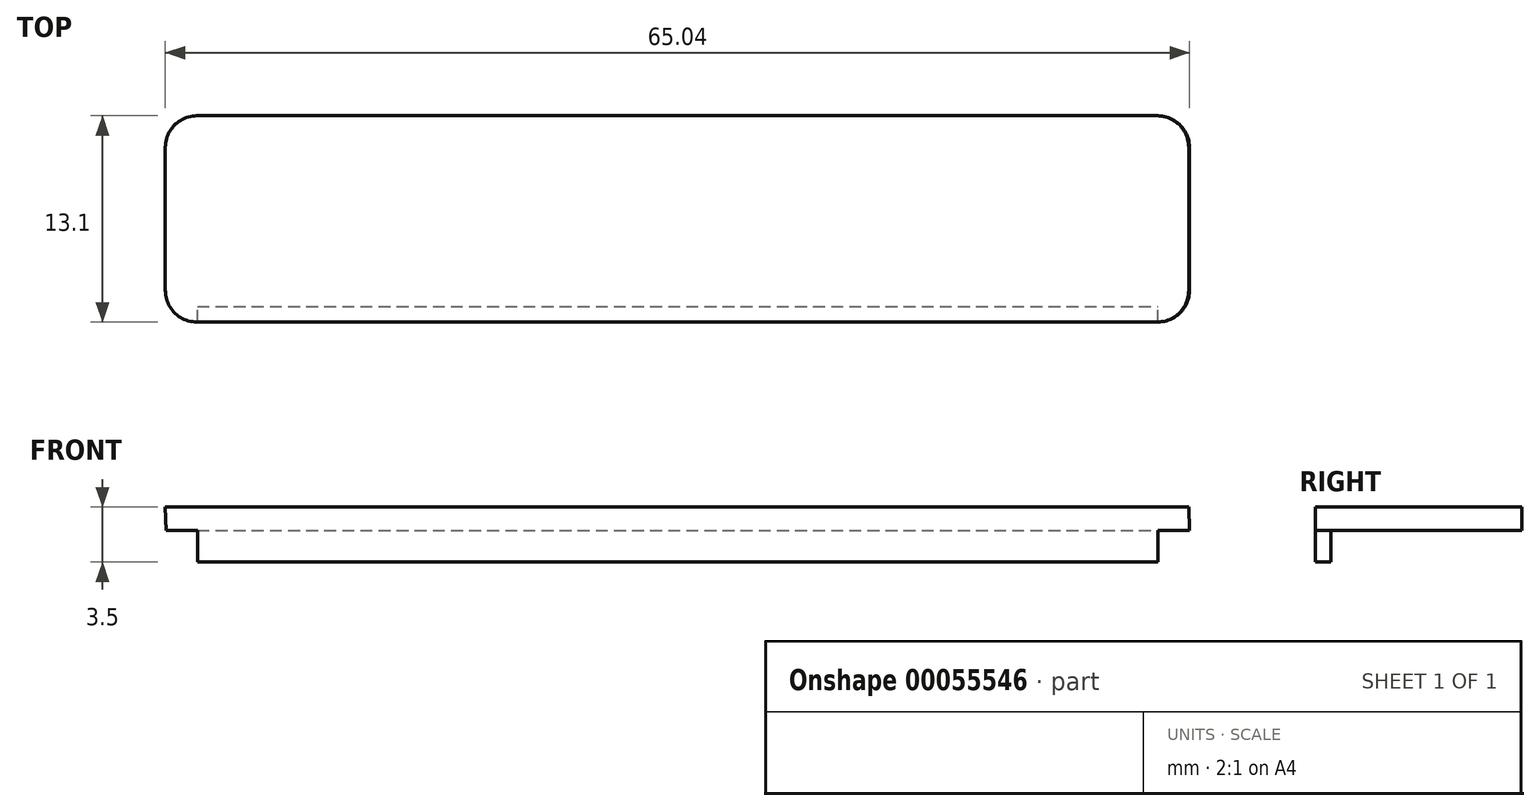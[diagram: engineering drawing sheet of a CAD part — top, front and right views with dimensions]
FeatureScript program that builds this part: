
annotation { "Feature Type Name" : "Feature", "Feature Type Description" : "" }
export const myFeature = defineFeature(function(context is Context, id is Id, definition is map)
    precondition{}
    {
        {
            var Q0;
            Q0=qCreatedBy(makeId("Front.planeOp"),FACE);
            var sketch = newSketch(context, id + "F0", { "sketchPlane" : qUnion([Q0])});
            skLineSegment(sketch, "E0", {"start": v(-42.25, 39.93) * mm, "end": v(22.75, 39.93) * mm});
            skLineSegment(sketch, "E1", {"start": v(-42.2, 38.43) * mm, "end": v(22.8, 38.43) * mm});
            skLineSegment(sketch, "E2", {"start": v(22.75, 39.93) * mm, "end": v(22.8, 38.43) * mm});
            skLineSegment(sketch, "E3", {"start": v(-42.25, 39.93) * mm, "end": v(-42.2, 38.43) * mm});
            skSolve(sketch);
        }
        {
            var Q0;
            {var subQ0=sQuery(id+"F0.wireOp",EDGE,"JaEvdv6h-OzHi-lbwa-UNxS-Qd7MtqvRkv5U");Q0=makeQuery(id+"F0.imprint","IMPRINT",FACE,{"disambiguationData":[TD([[makeQuery(id+"F0.imprint","IMPRINT",EDGE,{"derivedFrom":subQ0}),-1.0]])]});}
            var Q1;
            Q1=makeQuery(id+"F0.imprint","IMPRINT",FACE,{"disambiguationData":[TD([[makeQuery(id+"F0.imprint","IMPRINT",EDGE,{"derivedFrom":sQuery(id+"F0.wireOp",EDGE,"E1")}),1.0]])]});
            var Q2;
            {var subQ0=sQuery(id+"F0.wireOp",EDGE,"vx9o1PK7-6SiN-EeFp-MCv7-DjHtIqDTatKx");Q2=makeQuery(id+"F0.imprint","IMPRINT",FACE,{"disambiguationData":[TD([[makeQuery(id+"F0.imprint","IMPRINT",EDGE,{"derivedFrom":subQ0}),1.0]])]});}
            extrude(context, id + "F1", {"entities" : qUnion([Q0, Q1, Q2]), "depth" : 13.1 * mm});
        }
        {
            var Q0;
            Q0=makeQuery(id+"F1.opExtrude","SWEPT_FACE",FACE,{"disambiguationData":[OSD([sQuery(id+"F0.wireOp",EDGE,"E1")])]});
            var sketch = newSketch(context, id + "F2", { "sketchPlane" : qUnion([Q0])});
            skLineSegment(sketch, "E4.bottom", {"start": v(-40.2, 13.1) * mm, "end": v(20.8, 13.1) * mm});
            skLineSegment(sketch, "E4.top", {"start": v(-40.2, 12.1) * mm, "end": v(20.8, 12.1) * mm});
            skLineSegment(sketch, "E5", {"start": v(-40.2, 13.1) * mm, "end": v(-40.2, 12.1) * mm});
            skLineSegment(sketch, "E6", {"start": v(20.8, 13.1) * mm, "end": v(20.8, 12.1) * mm});
            skSolve(sketch);
        }
        {
            var Q0;
            Q0=makeQuery(id+"F1.opExtrude","CAP_EDGE",EDGE,{"disambiguationData":[OSD([sQuery(id+"F0.wireOp",EDGE,"E3")])],"isStart":false});
            var Q1;
            Q1=makeQuery(id+"F1.opExtrude","CAP_EDGE",EDGE,{"disambiguationData":[OSD([sQuery(id+"F0.wireOp",EDGE,"E2")])],"isStart":false});
            var Q2;
            Q2=makeQuery(id+"F1.opExtrude","CAP_EDGE",EDGE,{"disambiguationData":[OSD([sQuery(id+"F0.wireOp",EDGE,"E2")])],"isStart":true});
            var Q3;
            Q3=makeQuery(id+"F1.opExtrude","CAP_EDGE",EDGE,{"disambiguationData":[OSD([sQuery(id+"F0.wireOp",EDGE,"E3")])],"isStart":true});
            fillet(context, id + "F3", {"entities" : qUnion([Q0, Q1, Q2, Q3]), "radius" : 2 * mm, "tangentPropagation" : true, "allowEdgeOverflow" : false});
        }
        {
            var Q0;
            Q0=makeQuery(id+"F2.imprint","IMPRINT",FACE,{"disambiguationData":[TD([[makeQuery(id+"F2.imprint","IMPRINT",EDGE,{"derivedFrom":sQuery(id+"F2.wireOp",EDGE,"E4.bottom")}),-1.0]])]});
            extrude(context, id + "F4", {"entities" : qUnion([Q0]), "operationType" : NewBodyOperationType.ADD, "depth" : 2 * mm});
        }
    });
